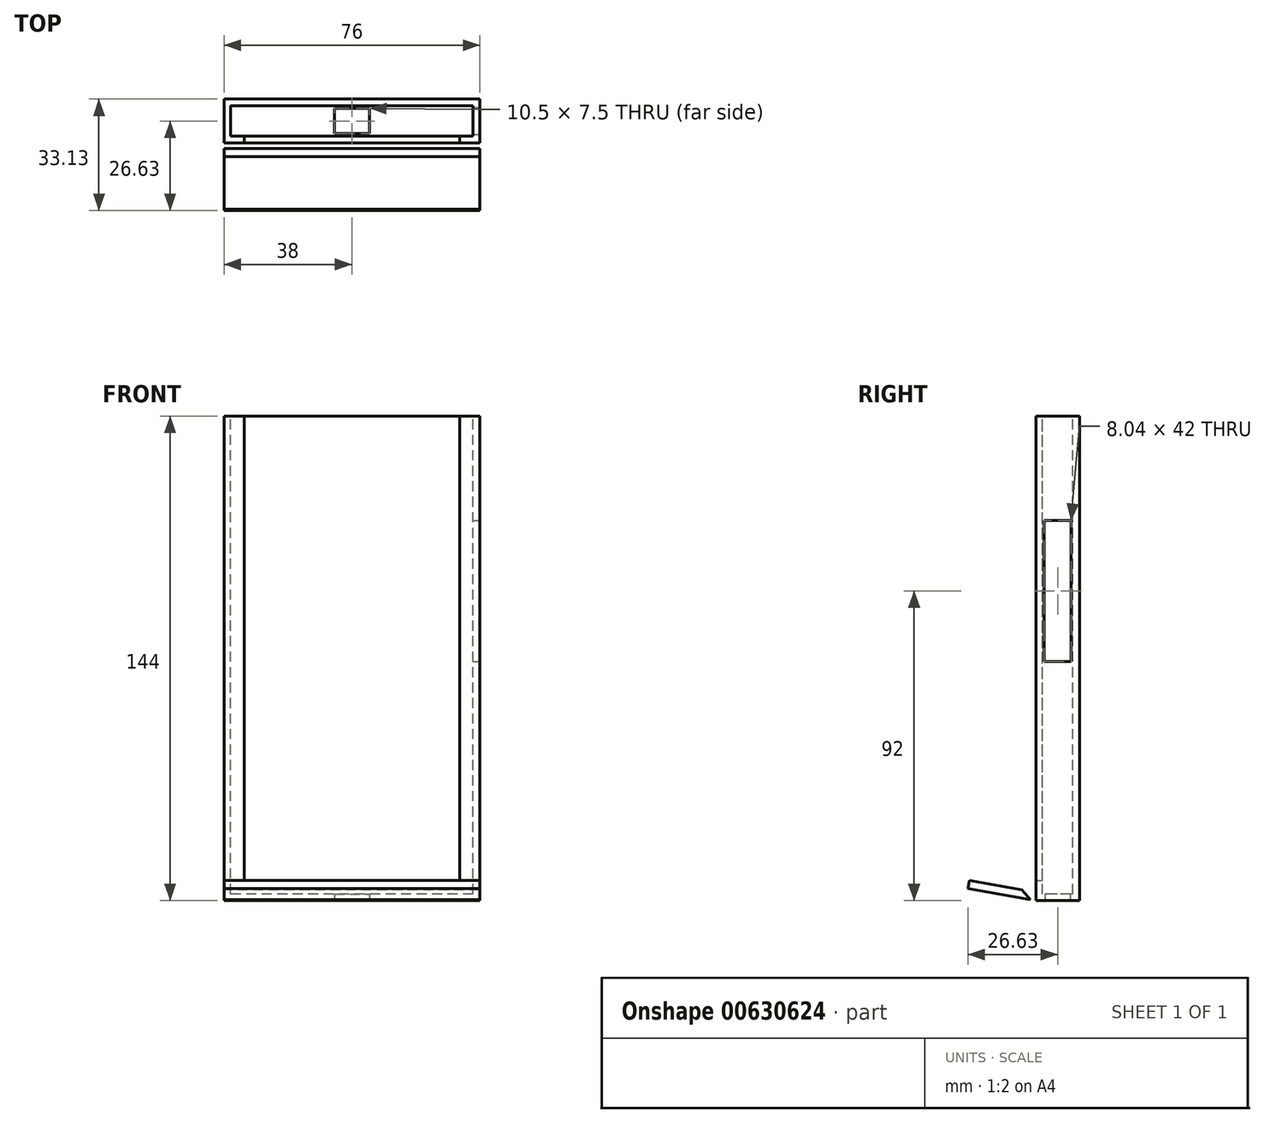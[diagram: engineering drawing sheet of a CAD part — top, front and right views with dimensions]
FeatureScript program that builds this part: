
annotation { "Feature Type Name" : "Feature", "Feature Type Description" : "" }
export const myFeature = defineFeature(function(context is Context, id is Id, definition is map)
    precondition{}
    {
        {
            var Q0;
            Q0=qCreatedBy(makeId("Front.planeOp"),FACE);
            var sketch = newSketch(context, id + "F0", { "sketchPlane" : qUnion([Q0])});
            skLineSegment(sketch, "E0.bottom", {"start": v(38, -72) * mm, "end": v(-38, -72) * mm});
            skLineSegment(sketch, "E0.top", {"start": v(38, 72) * mm, "end": v(-38, 72) * mm});
            skLineSegment(sketch, "E0.left", {"start": v(38, -72) * mm, "end": v(38, 72) * mm});
            skLineSegment(sketch, "E0.right", {"start": v(-38, -72) * mm, "end": v(-38, 72) * mm});
            skPoint(sketch, "E0.middle", {"position": v(0, 0) * mm});
            skSolve(sketch);
        }
        {
            var Q0;
            Q0=makeQuery(id+"F0.imprint","IMPRINT",FACE,{"disambiguationData":[TD([[makeQuery(id+"F0.imprint","IMPRINT",EDGE,{"derivedFrom":sQuery(id+"F0.wireOp",EDGE,"E0.bottom")}),-1.0]])]});
            extrude(context, id + "F1", {"entities" : qUnion([Q0]), "depth" : 13 * mm, "offsetDistance" : 25 * mm});
        }
        {
            var Q0;
            Q0=makeQuery(id+"F1.opExtrude","SWEPT_FACE",FACE,{"disambiguationData":[OSD([sQuery(id+"F0.wireOp",EDGE,"E0.top")])]});
            var sketch = newSketch(context, id + "F2", { "sketchPlane" : qUnion([Q0])});
            skLineSegment(sketch, "E1", {"start": v(-32, -13) * mm, "end": v(-32, -11) * mm});
            skLineSegment(sketch, "E2", {"start": v(-32, -11) * mm, "end": v(-36, -11) * mm});
            skLineSegment(sketch, "E3", {"start": v(-36, -11) * mm, "end": v(-36, -2) * mm});
            skLineSegment(sketch, "E4", {"start": v(-36, -2) * mm, "end": v(36, -2) * mm});
            skLineSegment(sketch, "E5", {"start": v(36, -2) * mm, "end": v(36, -11) * mm});
            skLineSegment(sketch, "E6", {"start": v(36, -11) * mm, "end": v(32, -11) * mm});
            skLineSegment(sketch, "E7", {"start": v(32, -11) * mm, "end": v(32, -13) * mm});
            skSolve(sketch);
        }
        {
            var Q0;
            {var subQ0=sQuery(id+"F2.wireOp",EDGE,"E1");Q0=makeQuery(id+"F2.imprint","IMPRINT",FACE,{"disambiguationData":[TD([[makeQuery(id+"F2.imprint","IMPRINT",EDGE,{"derivedFrom":subQ0}),-1.0]])]});}
            extrude(context, id + "F3", {"entities" : qUnion([Q0]), "operationType" : NewBodyOperationType.REMOVE, "oppositeDirection" : true, "depth" : 142 * mm, "offsetDistance" : 25 * mm});
        }
        {
            var Q0;
            Q0=makeQuery(id+"F3.boolean.opBoolean","COPY",FACE,{"derivedFrom":makeQuery(id+"F3.opExtrude","CAP_FACE",FACE,{"disambiguationData":[OSD([sQuery(id+"F0.wireOp",EDGE,"E0.top"),sQuery(id+"F2.wireOp",EDGE,"E1"),sQuery(id+"F2.wireOp",EDGE,"E2"),sQuery(id+"F2.wireOp",EDGE,"E3"),sQuery(id+"F2.wireOp",EDGE,"E4"),sQuery(id+"F2.wireOp",EDGE,"E5"),sQuery(id+"F2.wireOp",EDGE,"E6"),sQuery(id+"F2.wireOp",EDGE,"E7")])],"isStart":false})});
            var sketch = newSketch(context, id + "F4", { "sketchPlane" : qUnion([Q0])});
            skLineSegment(sketch, "E8", {"start": v(-32, -11) * mm, "end": v(32, -11) * mm});
            skSolve(sketch);
        }
        {
            var Q0;
            Q0=makeQuery(id+"F4.imprint","IMPRINT",FACE,{"disambiguationData":[TD([[makeQuery(id+"F4.imprint","IMPRINT",EDGE,{"derivedFrom":sQuery(id+"F4.wireOp",EDGE,"E8")}),-1.0]])]});
            extrude(context, id + "F5", {"entities" : qUnion([Q0]), "operationType" : NewBodyOperationType.ADD, "depth" : 4 * mm, "offsetDistance" : 25 * mm});
        }
        {
            var Q0;
            Q0=makeQuery(id+"F1.opExtrude","SWEPT_FACE",FACE,{"disambiguationData":[OSD([sQuery(id+"F0.wireOp",EDGE,"E0.bottom")])]});
            var sketch = newSketch(context, id + "F6", { "sketchPlane" : qUnion([Q0])});
            skPoint(sketch, "E9", {"position": v(0, 6.5) * mm});
            skLineSegment(sketch, "E10.bottom", {"start": v(5.25, 10.25) * mm, "end": v(-5.25, 10.25) * mm});
            skLineSegment(sketch, "E10.top", {"start": v(5.25, 2.75) * mm, "end": v(-5.25, 2.75) * mm});
            skLineSegment(sketch, "E10.left", {"start": v(5.25, 10.25) * mm, "end": v(5.25, 2.75) * mm});
            skLineSegment(sketch, "E10.right", {"start": v(-5.25, 10.25) * mm, "end": v(-5.25, 2.75) * mm});
            skSolve(sketch);
        }
        {
            var Q0;
            Q0=makeQuery(id+"F6.imprint","IMPRINT",FACE,{"disambiguationData":[TD([[makeQuery(id+"F6.imprint","IMPRINT",EDGE,{"derivedFrom":sQuery(id+"F6.wireOp",EDGE,"E10.bottom")}),1.0]])]});
            extrude(context, id + "F7", {"entities" : qUnion([Q0]), "operationType" : NewBodyOperationType.REMOVE, "oppositeDirection" : true, "depth" : 25 * mm, "offsetDistance" : 25 * mm});
        }
        {
            var Q0;
            Q0=makeQuery(id+"F1.opExtrude","SWEPT_FACE",FACE,{"disambiguationData":[OSD([sQuery(id+"F0.wireOp",EDGE,"E0.left")])]});
            var sketch = newSketch(context, id + "F8", { "sketchPlane" : qUnion([Q0])});
            skPoint(sketch, "E11", {"position": v(-6.5, 20) * mm});
            skLineSegment(sketch, "E12.bottom", {"start": v(-2.48, 41) * mm, "end": v(-10.52, 41) * mm});
            skLineSegment(sketch, "E12.top", {"start": v(-2.48, -1) * mm, "end": v(-10.52, -1) * mm});
            skLineSegment(sketch, "E12.left", {"start": v(-2.48, 41) * mm, "end": v(-2.48, -1) * mm});
            skLineSegment(sketch, "E12.right", {"start": v(-10.52, 41) * mm, "end": v(-10.52, -1) * mm});
            skSolve(sketch);
        }
        {
            var Q0;
            Q0=makeQuery(id+"F8.imprint","IMPRINT",FACE,{"disambiguationData":[TD([[makeQuery(id+"F8.imprint","IMPRINT",EDGE,{"derivedFrom":sQuery(id+"F8.wireOp",EDGE,"E12.bottom")}),1.0]])]});
            extrude(context, id + "F9", {"entities" : qUnion([Q0]), "operationType" : NewBodyOperationType.REMOVE, "oppositeDirection" : true, "depth" : 25 * mm, "offsetDistance" : 25 * mm});
        }
        {
            var Q0;
            Q0=makeQuery(id+"F1.opExtrude","SWEPT_FACE",FACE,{"disambiguationData":[OSD([sQuery(id+"F0.wireOp",EDGE,"E0.left")])]});
            var sketch = newSketch(context, id + "F10", { "sketchPlane" : qUnion([Q0])});
            skLineSegment(sketch, "E13", {"start": v(-13, -72) * mm, "end": v(-33.13, -68.45) * mm});
            skLineSegment(sketch, "E14", {"start": v(-33.13, -68.45) * mm, "end": v(-32.7, -65.99) * mm});
            skLineSegment(sketch, "E15", {"start": v(-32.7, -65.99) * mm, "end": v(-13, -69.46) * mm});
            skSolve(sketch);
        }
        {
            var Q0;
            {var subQ0=sQuery(id+"F10.wireOp",EDGE,"E13");Q0=makeQuery(id+"F10.imprint","IMPRINT",FACE,{"disambiguationData":[TD([[makeQuery(id+"F10.imprint","IMPRINT",EDGE,{"derivedFrom":subQ0}),-1.0]])]});}
            extrude(context, id + "F11", {"entities" : qUnion([Q0]), "oppositeDirection" : true, "depth" : 76 * mm, "offsetDistance" : 25 * mm});
        }
        {
            var Q0;
            Q0=makeQuery(id+"F11.opExtrude","SWEPT_EDGE",EDGE,{"disambiguationData":[OSD([sQuery(id+"F0.wireOp",EDGE,"E0.left"),sQuery(id+"F10.wireOp",EDGE,"E15")])]});
            chamfer(context, id + "F12", {"entities" : qUnion([Q0]), "width" : 5 * mm, "tangentPropagation" : true});
        }
    });
